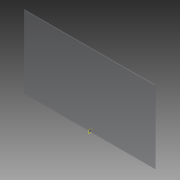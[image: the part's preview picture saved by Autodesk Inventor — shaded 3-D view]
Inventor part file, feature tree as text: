
AUTODESK INVENTOR PART (.ipt)
format: ipt  version: 2013 (Build 170138000, 138)  size: 69,120 bytes
history: native  units: in
note: dims shown in document units (in); Inventor stores cm internally (conversion verified against a paired STEP export)
features: extrude x1, plane x1, sketch x1
ambient origin geometry x8: Origin, YZ Plane, XZ Plane, XY Plane, X Axis, Y Axis, Z Axis, Center Point
bodies: Solid1 (feature_tree)
feature tree (3):
  extrude  "Extrusion1"  Depth=22.0in
  plane  "Work Plane1"
  sketch  "Sketch1"  dims[d0=39.75in d1=22.0in d2=0.125in d3=0.0in]
